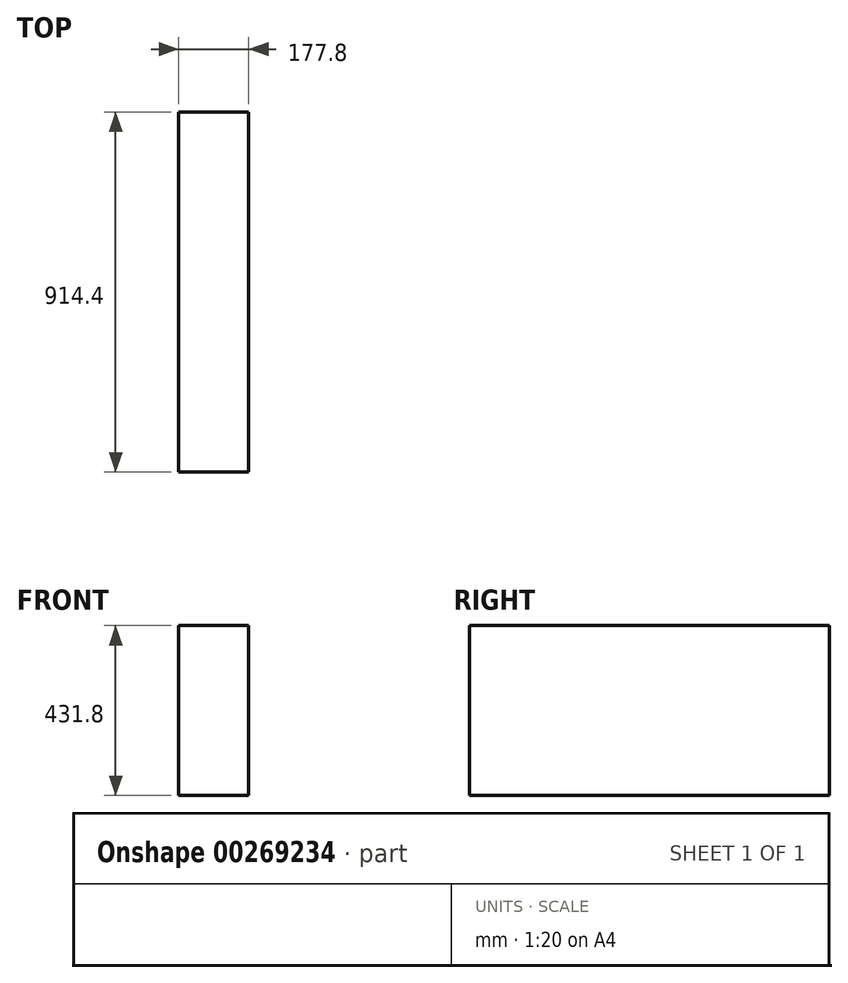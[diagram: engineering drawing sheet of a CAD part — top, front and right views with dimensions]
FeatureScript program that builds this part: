
annotation { "Feature Type Name" : "Feature", "Feature Type Description" : "" }
export const myFeature = defineFeature(function(context is Context, id is Id, definition is map)
    precondition{}
    {
        {
            var Q0;
            Q0=qCreatedBy(makeId("Front.planeOp"),FACE);
            var sketch = newSketch(context, id + "F0", { "sketchPlane" : qUnion([Q0])});
            skLineSegment(sketch, "E0.bottom", {"start": v(0, 0) * mm, "end": v(177.8, 0) * mm});
            skLineSegment(sketch, "E0.top", {"start": v(0, 431.8) * mm, "end": v(177.8, 431.8) * mm});
            skLineSegment(sketch, "E0.left", {"start": v(0, 0) * mm, "end": v(0, 431.8) * mm});
            skLineSegment(sketch, "E0.right", {"start": v(177.8, 0) * mm, "end": v(177.8, 431.8) * mm});
            skSolve(sketch);
        }
        {
            var Q0;
            Q0 = qSketchRegion(id + "F0", true);
            extrude(context, id + "F1", {"entities" : qUnion([Q0]), "depth" : 914.4 * mm});
        }
    });
